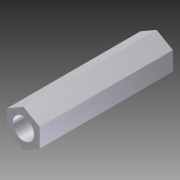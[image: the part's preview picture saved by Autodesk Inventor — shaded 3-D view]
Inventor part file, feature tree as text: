
AUTODESK INVENTOR PART (.ipt)
format: ipt  version: 2012 (Build 160160000, 160)  size: 77,312 bytes
history: native  units: in
note: dims shown in document units (in); Inventor stores cm internally (conversion verified against a paired STEP export)
features: extrude x1, sketch x1
ambient origin geometry x8: Origin, YZ Plane, XZ Plane, XY Plane, X Axis, Y Axis, Z Axis, Center Point
bodies: Solid1 (feature_tree)
feature tree (2):
  extrude  "Extrusion1"  Depth=0.3in
  sketch  "Sketch1"  dims[d0=0.2in d1=0.3in d2=1.25in d3=0.0in]
